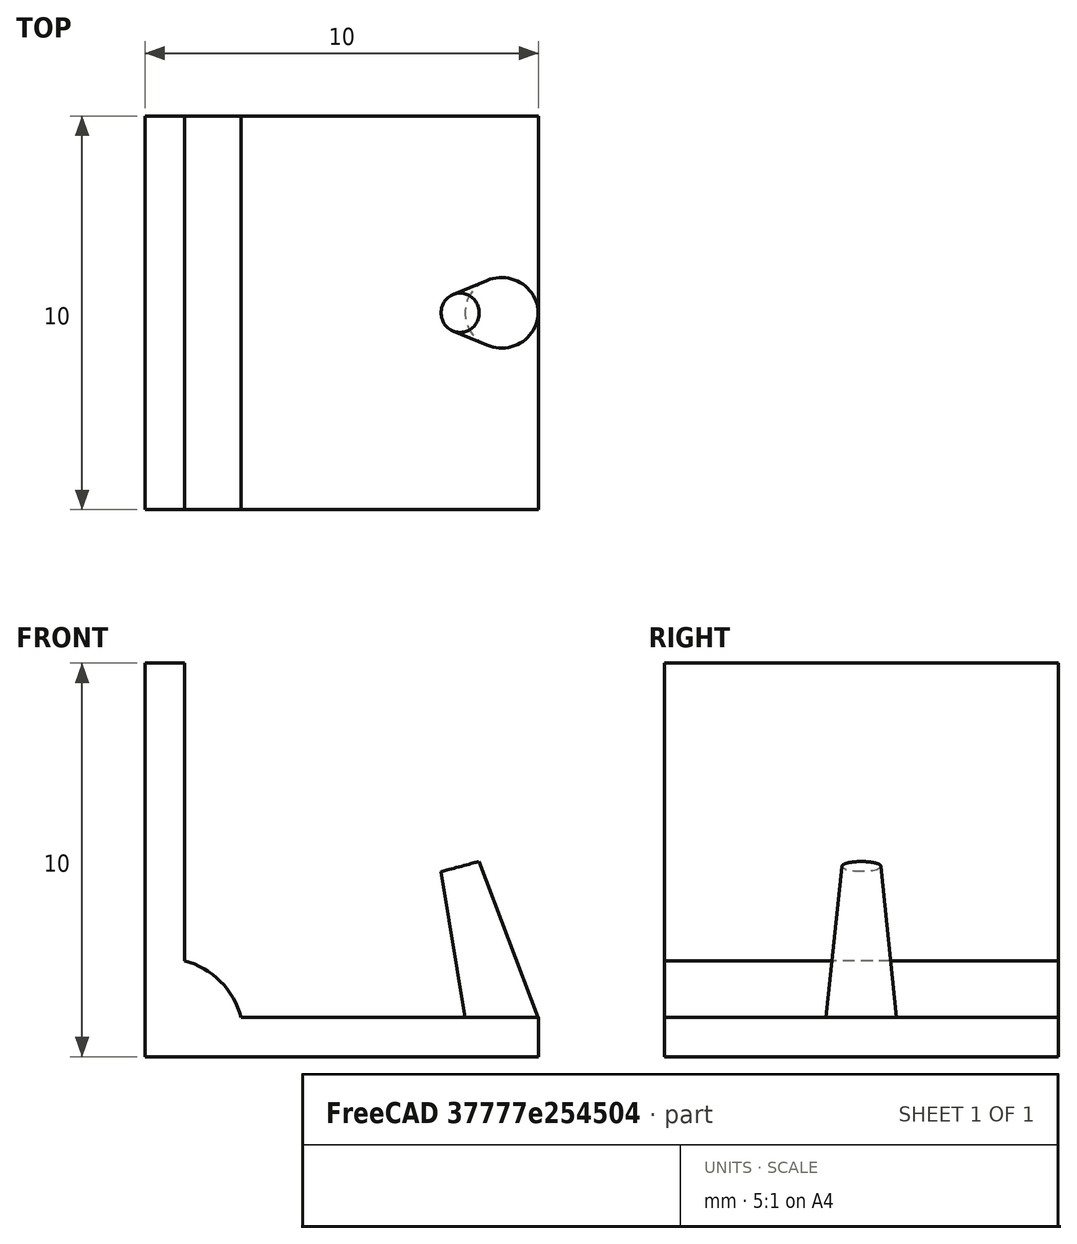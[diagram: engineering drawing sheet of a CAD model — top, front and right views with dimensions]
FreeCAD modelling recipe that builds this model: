
FCSTD DOCUMENT  (FreeCAD 0.16R6712 (Git))
Label: Gancho_calendario
License: CreativeCommons Attribution-ShareAlike
LicenseURL: http://creativecommons.org/licenses/by-sa/4.0/
objects: Part::Box×5, Part::Cut×3, Part::Cone×1, Part::Cylinder×1, Part::MultiFuse×1
note: 11 computed .brp shape members not serialized (recipe doc carries the construction recipe); baked Part::Feature solids carry a one-line shape summary decoded from their .brp

FEATURE [Part::Box] Box  label="Cubo"
  Height = 1
  Length = 10
  Width = 10
FEATURE [Part::Box] Box001  label="Cubo001"
  Height = 10
  Length = 1
  Width = 10
FEATURE [Part::Cone] Cone  label="Cono"
  Angle = 360
  Height = 5
  Placement = pos=(9.3,5,0) rot=(0,-1,0;0.261799rad)
  Radius1 = 1
  Radius2 = 0.5
FEATURE [Part::Cylinder] Cylinder  label="Cilindro"
  Angle = 360
  Height = 10
  Placement = pos=(0.5,10,0.5) rot=(1,0,0;1.5708rad)
  Radius = 2
FEATURE [Part::Box] Box002  label="Cubo002"
  Height = 2
  Length = 15
  Placement = pos=(-3,0,-2) rot=(0,0,1;0rad)
  Width = 10
FEATURE [Part::Box] Box003  label="Cubo003"
  Height = 10
  Length = 3
  Placement = pos=(-3,0,0) rot=(0,0,1;0rad)
  Width = 10
FEATURE [Part::Box] Box004  label="Cubo004"
  Height = 1
  Length = 2
  Placement = pos=(10,0,0) rot=(0,0,1;0rad)
  Width = 10
FEATURE [Part::MultiFuse] Fusion
  Shapes = -> [Box,Box001,Cone,Cylinder]
FEATURE [Part::Cut] Cut
  Base = -> Fusion
  Tool = -> Box004
FEATURE [Part::Cut] Cut001
  Base = -> Cut
  Tool = -> Box003
FEATURE [Part::Cut] Cut002
  Base = -> Cut001
  Tool = -> Box002
